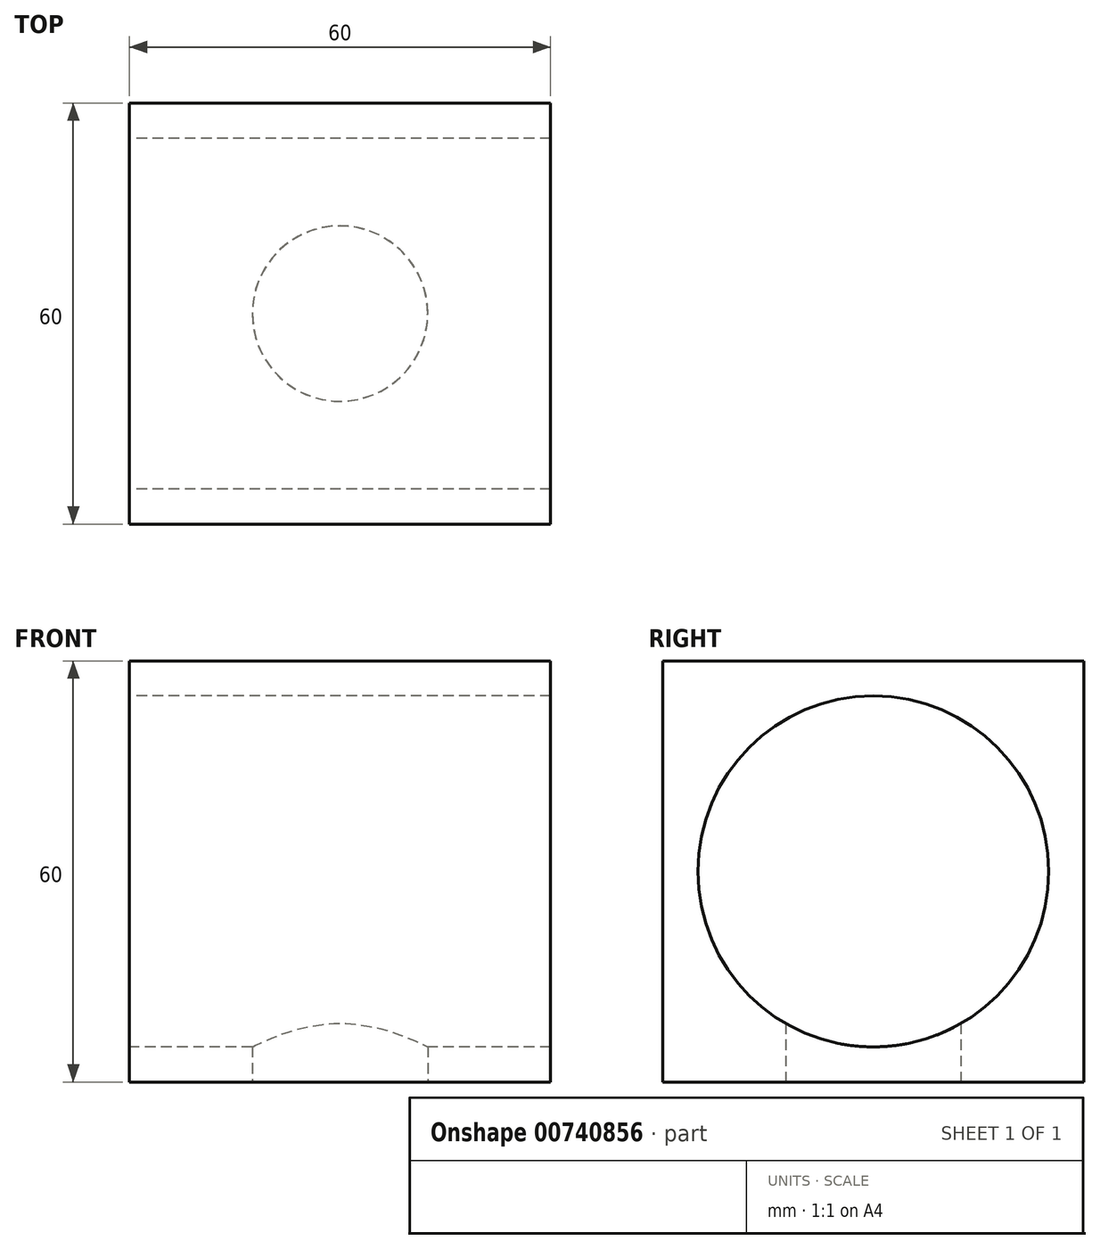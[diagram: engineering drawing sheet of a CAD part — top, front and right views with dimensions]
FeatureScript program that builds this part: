
annotation { "Feature Type Name" : "Feature", "Feature Type Description" : "" }
export const myFeature = defineFeature(function(context is Context, id is Id, definition is map)
    precondition{}
    {
        {
            var Q0;
            Q0=qCreatedBy(makeId("Right.planeOp"),FACE);
            var sketch = newSketch(context, id + "F0", { "sketchPlane" : qUnion([Q0])});
            skCircle(sketch, "E0", {"center": v(0, 0) * mm, "radius": 25 * mm});
            skLineSegment(sketch, "E1.bottom", {"start": v(-30, -30) * mm, "end": v(30, -30) * mm});
            skLineSegment(sketch, "E1.top", {"start": v(-30, 30) * mm, "end": v(30, 30) * mm});
            skLineSegment(sketch, "E1.left", {"start": v(-30, -30) * mm, "end": v(-30, 30) * mm});
            skLineSegment(sketch, "E1.right", {"start": v(30, -30) * mm, "end": v(30, 30) * mm});
            skSolve(sketch);
        }
        {
            var Q0;
            Q0 = qSketchRegion(id + "F0", true);
            extrude(context, id + "F1", {"entities" : qUnion([Q0]), "endBound" : BoundingType.SYMMETRIC, "depth" : 60 * mm, "offsetDistance" : 25 * mm});
        }
        {
            var Q0;
            Q0=makeQuery(id+"F1.opExtrude","SWEPT_FACE",FACE,{"disambiguationData":[OSD([sQuery(id+"F0.wireOp",EDGE,"E1.bottom")])]});
            var sketch = newSketch(context, id + "F2", { "sketchPlane" : qUnion([Q0])});
            skCircle(sketch, "E2", {"center": v(0, 0) * mm, "radius": 12.5 * mm});
            skSolve(sketch);
        }
        {
            var Q0;
            Q0 = qSketchRegion(id + "F2", true);
            extrude(context, id + "F3", {"entities" : qUnion([Q0]), "operationType" : NewBodyOperationType.REMOVE, "oppositeDirection" : true, "depth" : 25 * mm, "offsetDistance" : 25 * mm, "hasSecondDirection" : true, "secondDirectionOppositeDirection" : false, "secondDirectionDepth" : 25 * mm});
        }
    });
